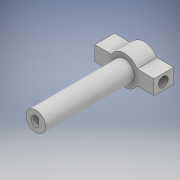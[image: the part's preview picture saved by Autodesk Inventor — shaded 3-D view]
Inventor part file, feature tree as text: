
AUTODESK INVENTOR PART (.ipt)
format: ipt  version: 2017 (Build 210142000, 142)  size: 142,336 bytes
history: native  units: mm
features: extrude x5, sketch x5, thread x1
ambient origin geometry x8: Origin, YZ Plane, XZ Plane, XY Plane, X Axis, Y Axis, Z Axis, Center Point
bodies: Body1 (feature_tree)
feature tree (11):
  extrude  "Extrusion3"  Depth=15.0mm
  extrude  "Extrusion5"  Depth=3.75mm
  extrude  "Extrusion6"  Depth=30.0mm
  extrude  "Extrusion9"  Depth=10.0mm TaperAngle=0.0deg
  extrude  "Extrusion10"  Depth=45.0mm TaperAngle=0.0deg
  thread  "Thread2"  [1 undecoded]
  sketch  "Sketch3"  dims[d27=15.0mm d28=15.0mm]
  sketch  "Sketch5"  dims[d29=0.0mm d30=3.75mm]
  sketch  "Sketch6"  dims[d31=90.0deg d32=30.0mm]
  sketch  "Sketch7"  dims[d33=7.5mm d34=10.0mm d35=0.0mm]
  sketch  "Sketch8"  dims[d39=10.0mm d42=45.0mm d43=0.0mm d44=5.0mm d45=60.0mm d46=0.0mm d50=1.0mm d51=180.0deg d56=55.0mm d57=0.0mm d58=5.0mm d59=15.0mm d60=0.0mm d61=10.0mm d62=0.0mm]
note: 1 required parameter value undecoded (feature->parameter linkage not recoverable at this tier; creation-order binding heuristic only, values carry confidence <= 0.55)
